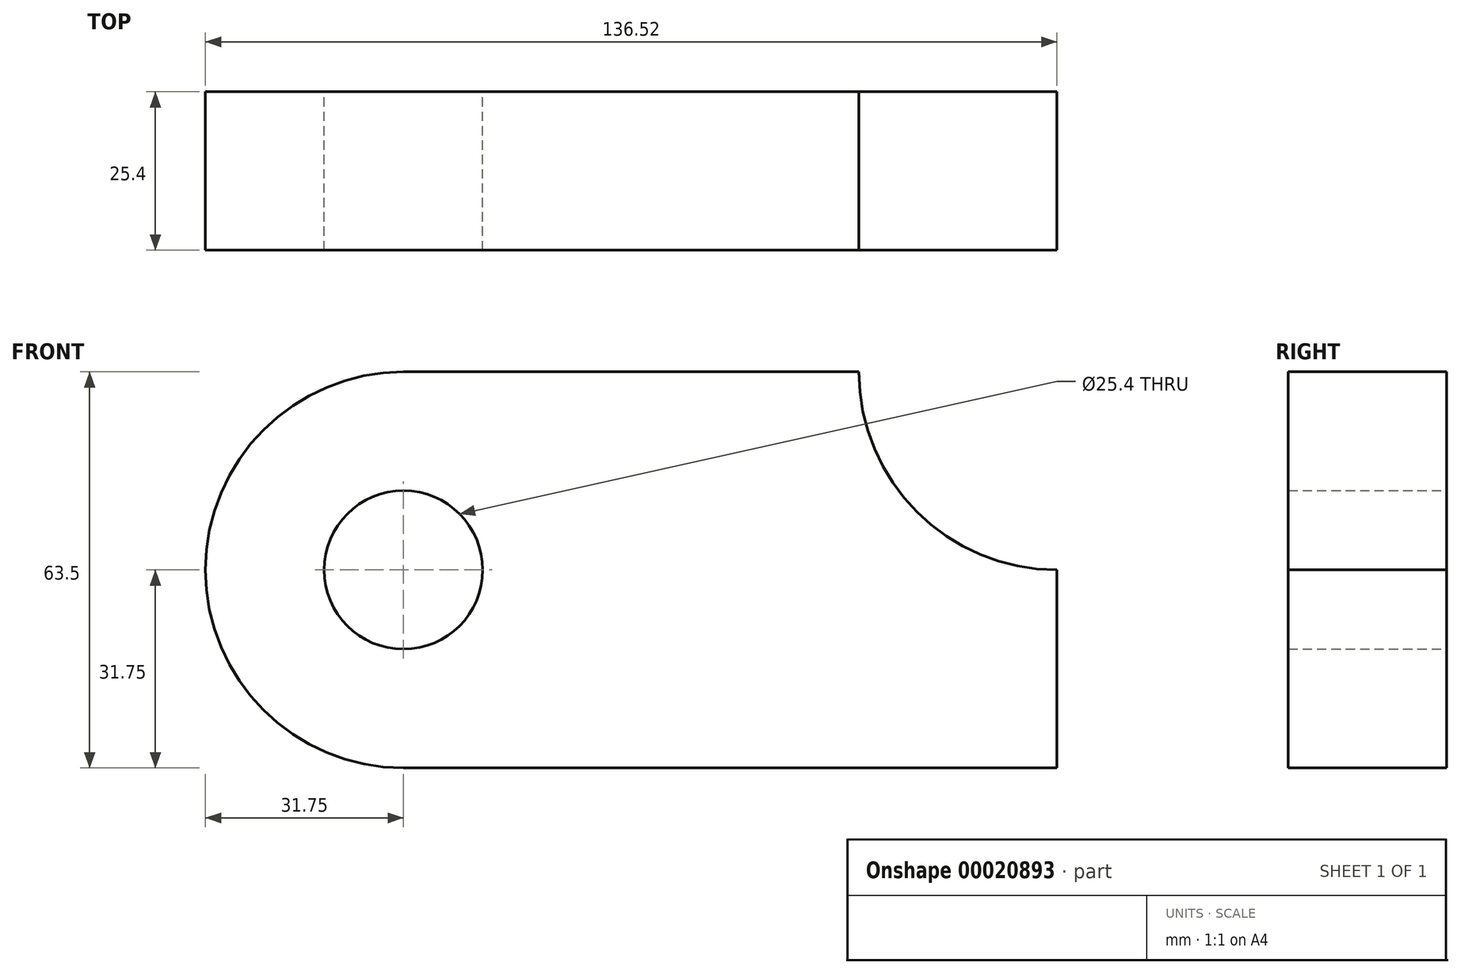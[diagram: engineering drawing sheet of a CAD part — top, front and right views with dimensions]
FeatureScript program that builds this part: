
annotation { "Feature Type Name" : "Feature", "Feature Type Description" : "" }
export const myFeature = defineFeature(function(context is Context, id is Id, definition is map)
    precondition{}
    {
        {
            var Q0;
            Q0=qCreatedBy(makeId("Front.planeOp"),FACE);
            var sketch = newSketch(context, id + "F0", { "sketchPlane" : qUnion([Q0])});
            skLineSegment(sketch, "E0.bottom", {"start": v(0, 0) * mm, "end": v(73.03, 0) * mm});
            skLineSegment(sketch, "E0.top", {"start": v(0, -63.5) * mm, "end": v(104.78, -63.5) * mm});
            skLineSegment(sketch, "E0.right", {"start": v(104.78, -31.75) * mm, "end": v(104.78, -63.5) * mm});
            skArc(sketch, "E1", {"start": v(0, 0) * mm, "mid": v(-31.75, -31.75) * mm, "end": v(0, -63.5) * mm});
            skCircle(sketch, "E2", {"center": v(0, -31.75) * mm, "radius": 12.7 * mm});
            skArc(sketch, "E3", {"start": v(73.03, 0) * mm, "mid": v(82.32, -22.45) * mm, "end": v(104.78, -31.75) * mm});
            skSolve(sketch);
        }
        {
            var Q0;
            Q0 = qSketchRegion(id + "F0", true);
            extrude(context, id + "F1", {"entities" : qUnion([Q0]), "depth" : 25.4 * mm});
        }
    });
